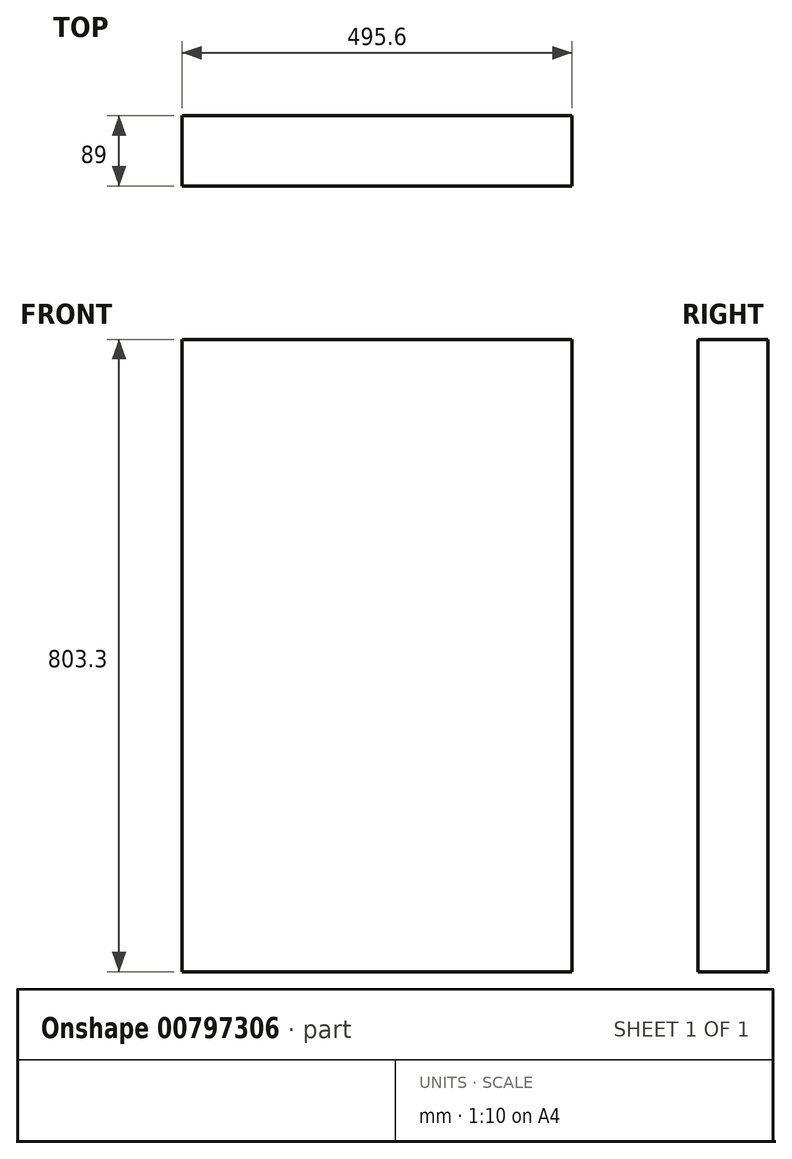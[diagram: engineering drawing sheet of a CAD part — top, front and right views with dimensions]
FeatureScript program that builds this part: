
annotation { "Feature Type Name" : "Feature", "Feature Type Description" : "" }
export const myFeature = defineFeature(function(context is Context, id is Id, definition is map)
    precondition{}
    {
        {
            var Q0;
            Q0=qCreatedBy(makeId("Front.planeOp"),FACE);
            var sketch = newSketch(context, id + "F0", { "sketchPlane" : qUnion([Q0])});
            skLineSegment(sketch, "E0.bottom", {"start": v(247.8, 401.65) * mm, "end": v(-247.8, 401.65) * mm});
            skLineSegment(sketch, "E0.top", {"start": v(247.8, -401.65) * mm, "end": v(-247.8, -401.65) * mm});
            skLineSegment(sketch, "E0.left", {"start": v(247.8, 401.65) * mm, "end": v(247.8, -401.65) * mm});
            skLineSegment(sketch, "E0.right", {"start": v(-247.8, 401.65) * mm, "end": v(-247.8, -401.65) * mm});
            skPoint(sketch, "E0.middle", {"position": v(0, 0) * mm});
            skSolve(sketch);
        }
        {
            var Q0;
            Q0=qSketchRegion(id+"F0",true);
            extrude(context, id + "F1", {"entities" : qUnion([Q0]), "depth" : 89 * mm, "offsetDistance" : 25 * mm, "symmetric" : true});
        }
    });
